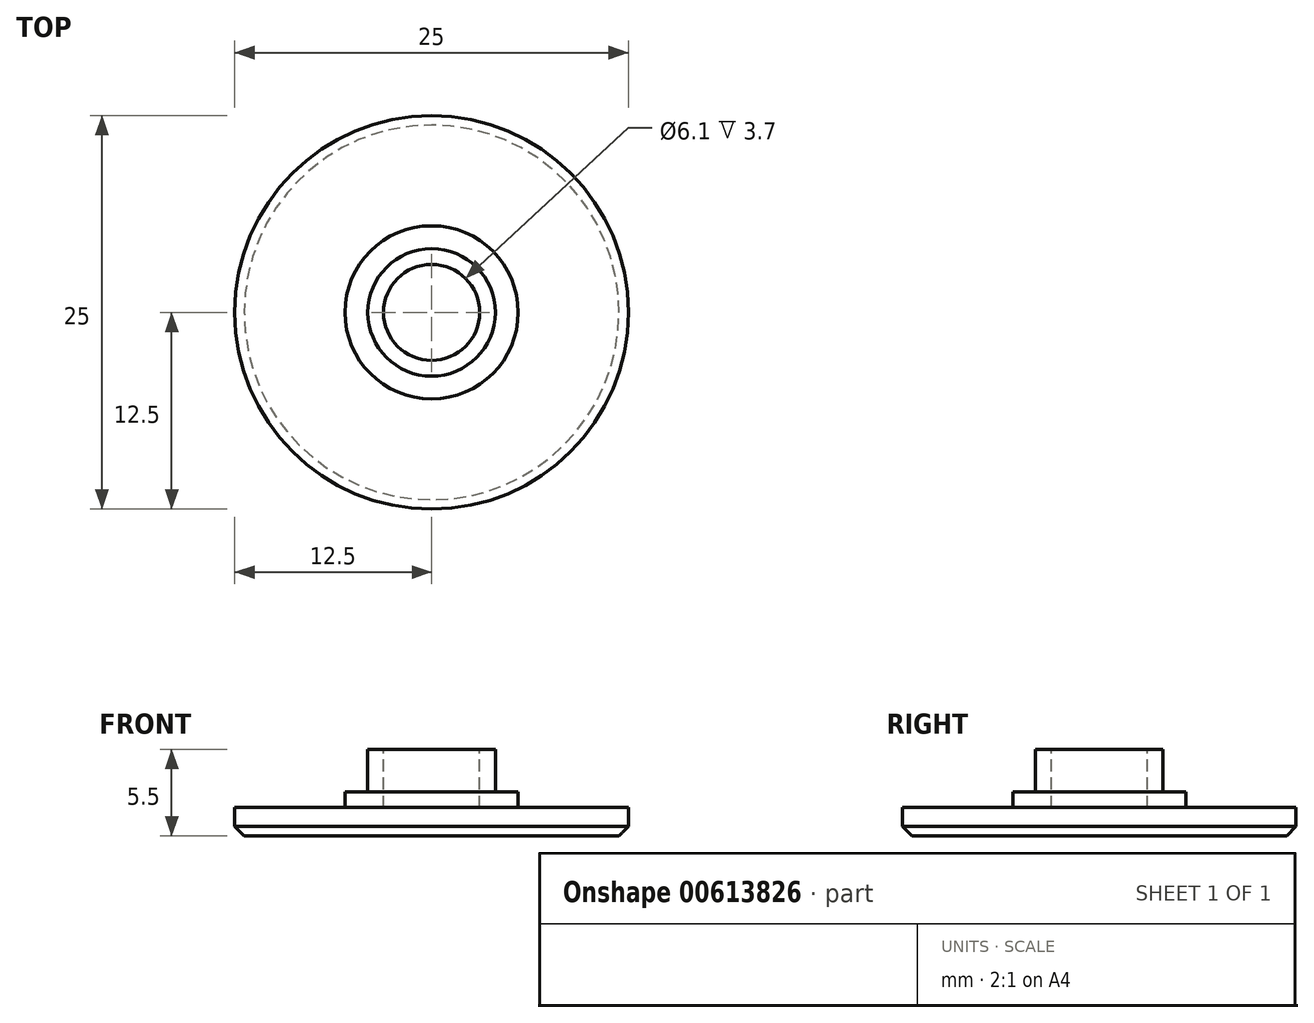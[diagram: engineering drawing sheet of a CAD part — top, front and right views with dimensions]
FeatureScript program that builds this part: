
annotation { "Feature Type Name" : "Feature", "Feature Type Description" : "" }
export const myFeature = defineFeature(function(context is Context, id is Id, definition is map)
    precondition{}
    {
        {
            var Q0;
            Q0=qCreatedBy(makeId("Top.planeOp"),FACE);
            var sketch = newSketch(context, id + "F0", { "sketchPlane" : qUnion([Q0])});
            skCircle(sketch, "E0", {"center": v(0, 0) * mm, "radius": 12.5 * mm});
            skCircle(sketch, "E1", {"center": v(0, 0) * mm, "radius": 5.5 * mm});
            skCircle(sketch, "E2", {"center": v(0, 0) * mm, "radius": 4.05 * mm});
            skSolve(sketch);
        }
        {
            var Q0;
            Q0 = qSketchRegion(id + "F0", true);
            var Q1;
            Q1=makeQuery(id+"F0.imprint","IMPRINT",FACE,{"disambiguationData":[TD([[makeQuery(id+"F0.imprint","IMPRINT",EDGE,{"derivedFrom":sQuery(id+"F0.wireOp",EDGE,"E1")}),1.0]])]});
            var Q2;
            Q2=makeQuery(id+"F0.imprint","IMPRINT",FACE,{"disambiguationData":[TD([[makeQuery(id+"F0.imprint","IMPRINT",EDGE,{"derivedFrom":sQuery(id+"F0.wireOp",EDGE,"E2")}),1.0]])]});
            extrude(context, id + "F1", {"entities" : qUnion([Q0, Q1, Q2]), "depth" : 1.8 * mm, "offsetDistance" : 25 * mm});
        }
        {
            var Q0;
            Q0=makeQuery(id+"F0.imprint","IMPRINT",FACE,{"disambiguationData":[TD([[makeQuery(id+"F0.imprint","IMPRINT",EDGE,{"derivedFrom":sQuery(id+"F0.wireOp",EDGE,"E1")}),1.0]])]});
            extrude(context, id + "F2", {"entities" : qUnion([Q0]), "operationType" : NewBodyOperationType.ADD, "depth" : 2.8 * mm, "offsetDistance" : 25 * mm});
        }
        {
            var Q0;
            Q0=makeQuery(id+"F0.imprint","IMPRINT",FACE,{"disambiguationData":[TD([[makeQuery(id+"F0.imprint","IMPRINT",EDGE,{"derivedFrom":sQuery(id+"F0.wireOp",EDGE,"E2")}),1.0]])]});
            extrude(context, id + "F3", {"entities" : qUnion([Q0]), "operationType" : NewBodyOperationType.ADD, "depth" : 5.5 * mm, "offsetDistance" : 25 * mm});
        }
        {
            var Q0;
            Q0=makeQuery(id+"F3.opExtrude","CAP_FACE",FACE,{"disambiguationData":[OSD([sQuery(id+"F0.wireOp",EDGE,"E2")])],"isStart":false});
            var sketch = newSketch(context, id + "F4", { "sketchPlane" : qUnion([Q0])});
            skCircle(sketch, "E3.0", {"center": v(0, 0) * mm, "radius": 3.05 * mm});
            skSolve(sketch);
        }
        {
            var Q0;
            Q0 = qSketchRegion(id + "F4", true);
            var Q1;
            {var subQ0=sQuery(id+"F0.wireOp",EDGE,"E0");Q1=makeQuery(id+"F2.boolean.opBoolean","SPLIT",FACE,{"disambiguationData":[TD([makeQuery(id+"F1.opExtrude","SWEPT_FACE",FACE,{"disambiguationData":[OSD([subQ0])]})])],"derivedFrom":makeQuery(id+"F1.opExtrude","CAP_FACE",FACE,{"disambiguationData":[OSD([subQ0])],"isStart":false})});}
            extrude(context, id + "F5", {"entities" : qUnion([Q0]), "operationType" : NewBodyOperationType.REMOVE, "endBound" : BoundingType.UP_TO_SURFACE, "oppositeDirection" : true, "depth" : 25 * mm, "endBoundEntityFace" : qUnion([Q1]), "offsetDistance" : 25 * mm});
        }
        {
            var Q0;
            Q0=makeQuery(id+"F1.opExtrude","CAP_EDGE",EDGE,{"disambiguationData":[OSD([sQuery(id+"F0.wireOp",EDGE,"E0")])],"isStart":true});
            chamfer(context, id + "F6", {"entities" : qUnion([Q0]), "width" : 0.6 * mm, "tangentPropagation" : true});
        }
    });
